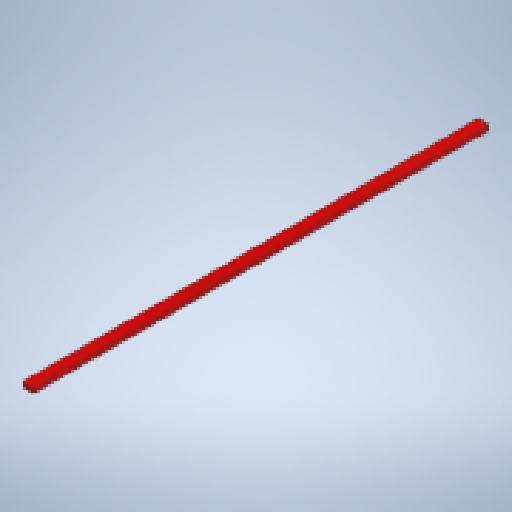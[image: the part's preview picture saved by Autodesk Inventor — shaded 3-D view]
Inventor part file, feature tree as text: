
AUTODESK INVENTOR PART (.ipt)
format: ipt  version: 2025.1 (Build 291241020, 241B)  size: 138,752 bytes
history: native  units: in
note: dims shown in document units (in); Inventor stores cm internally (conversion verified against a paired STEP export)
features: extrude x1, sketch x1, other x1
ambient origin geometry x8: Origin, YZ Plane, XZ Plane, XY Plane, X Axis, Y Axis, Z Axis, Center Point
bodies: Solid1 (feature_tree)
feature tree (3):
  extrude  "Extrusion1"  Depth=1.5in
  sketch  "Sketch1"  dims[d0=3.5in d1=1.5in d2=144.0in d3=0.0in]
  other  "Finish1"
